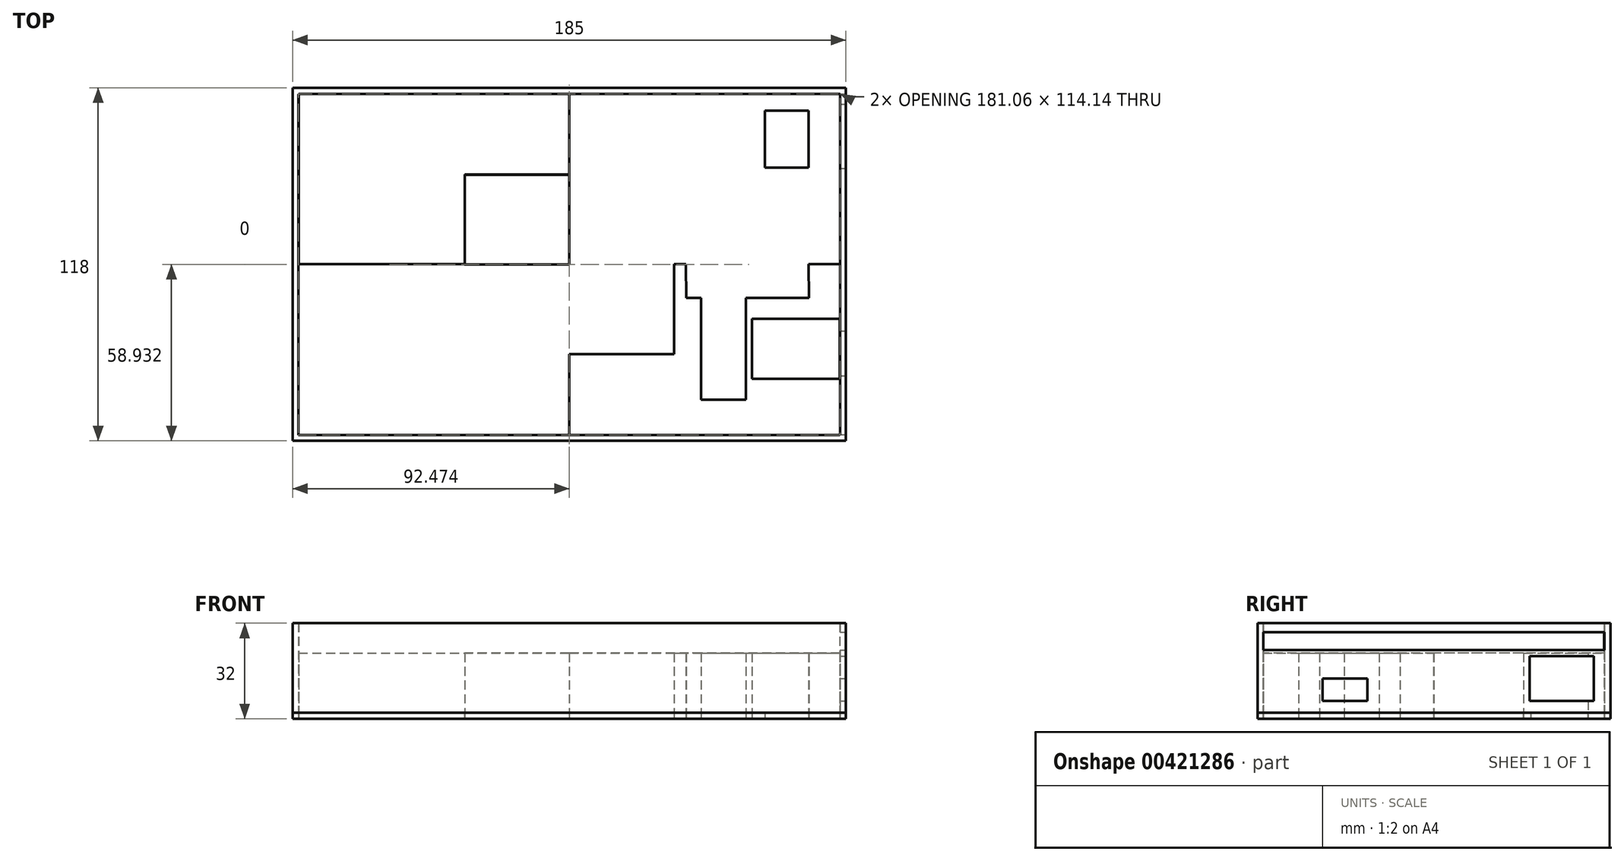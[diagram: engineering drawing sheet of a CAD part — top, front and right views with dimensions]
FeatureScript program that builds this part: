
annotation { "Feature Type Name" : "Feature", "Feature Type Description" : "" }
export const myFeature = defineFeature(function(context is Context, id is Id, definition is map)
    precondition{}
    {
        {
            var Q0;
            Q0=qCreatedBy(makeId("Top.planeOp"),FACE);
            var sketch = newSketch(context, id + "F0", { "sketchPlane" : qUnion([Q0])});
            skLineSegment(sketch, "E0.bottom", {"start": v(-155.12, 118) * mm, "end": v(29.88, 118) * mm});
            skLineSegment(sketch, "E0.top", {"start": v(-155.12, 0) * mm, "end": v(29.88, 0) * mm});
            skLineSegment(sketch, "E0.left", {"start": v(-155.12, 118) * mm, "end": v(-155.12, 0) * mm});
            skLineSegment(sketch, "E0.right", {"start": v(29.88, 118) * mm, "end": v(29.88, 0) * mm});
            skLineSegment(sketch, "E1.left", {"start": v(27.88, 108.58) * mm, "end": v(27.88, 9.42) * mm});
            skLineSegment(sketch, "E1.right", {"start": v(-153.12, 108.58) * mm, "end": v(-153.12, 9.42) * mm});
            skPoint(sketch, "E1.middle", {"position": v(-62.62, 59) * mm});
            skLineSegment(sketch, "E2", {"start": v(-153.12, 59) * mm, "end": v(-153.12, 116) * mm});
            skLineSegment(sketch, "E3", {"start": v(-153.12, 116) * mm, "end": v(27.88, 116) * mm});
            skLineSegment(sketch, "E4", {"start": v(27.88, 116) * mm, "end": v(27.88, 108.58) * mm});
            skLineSegment(sketch, "E5", {"start": v(-153.12, 59) * mm, "end": v(-153.12, 2) * mm});
            skLineSegment(sketch, "E6", {"start": v(-153.12, 2) * mm, "end": v(27.88, 2) * mm});
            skLineSegment(sketch, "E7", {"start": v(27.88, 2) * mm, "end": v(27.88, 9.42) * mm});
            skLineSegment(sketch, "E8.bottom", {"start": v(-153.17, 115.86) * mm, "end": v(27.83, 115.86) * mm});
            skLineSegment(sketch, "E8.top", {"start": v(-153.17, 1.86) * mm, "end": v(27.83, 1.86) * mm});
            skLineSegment(sketch, "E8.left", {"start": v(-153.17, 115.86) * mm, "end": v(-153.17, 1.86) * mm});
            skLineSegment(sketch, "E8.right", {"start": v(27.83, 115.86) * mm, "end": v(27.83, 1.86) * mm});
            skLineSegment(sketch, "E9", {"start": v(-153.17, 58.86) * mm, "end": v(27.83, 58.86) * mm});
            skLineSegment(sketch, "E10", {"start": v(-62.67, 1.86) * mm, "end": v(-62.67, 115.86) * mm});
            skLineSegment(sketch, "E11", {"start": v(-62.67, 1.86) * mm, "end": v(-62.67, 58.86) * mm});
            skPoint(sketch, "E12.middle", {"position": v(-62.67, 58.86) * mm});
            skLineSegment(sketch, "E13", {"start": v(-62.67, 58.86) * mm, "end": v(-27.67, 58.86) * mm});
            skLineSegment(sketch, "E14", {"start": v(-62.67, 58.86) * mm, "end": v(-62.67, 28.86) * mm});
            skLineSegment(sketch, "E15", {"start": v(-27.67, 28.86) * mm, "end": v(-27.67, 88.86) * mm});
            skLineSegment(sketch, "E16", {"start": v(-27.67, 88.86) * mm, "end": v(-97.67, 88.86) * mm});
            skLineSegment(sketch, "E17", {"start": v(-97.67, 88.86) * mm, "end": v(-97.67, 28.86) * mm});
            skLineSegment(sketch, "E18", {"start": v(-97.67, 28.86) * mm, "end": v(-27.67, 28.86) * mm});
            skLineSegment(sketch, "E19", {"start": v(-27.67, 58.86) * mm, "end": v(27.83, 58.86) * mm});
            skLineSegment(sketch, "E20", {"start": v(-23.67, 58.86) * mm, "end": v(-27.67, 58.86) * mm});
            skLineSegment(sketch, "E21", {"start": v(17.33, 58.86) * mm, "end": v(-23.67, 58.86) * mm});
            skLineSegment(sketch, "E22", {"start": v(17.33, 82.72) * mm, "end": v(17.33, 58.86) * mm});
            skLineSegment(sketch, "E23", {"start": v(-23.67, 58.86) * mm, "end": v(-23.67, 82.72) * mm});
            skLineSegment(sketch, "E24", {"start": v(-23.67, 82.72) * mm, "end": v(17.33, 82.72) * mm});
            skLineSegment(sketch, "E25", {"start": v(-18.54, 13.72) * mm, "end": v(-3.54, 13.72) * mm});
            skLineSegment(sketch, "E26", {"start": v(-18.54, 13.72) * mm, "end": v(-18.54, 47.72) * mm});
            skLineSegment(sketch, "E27", {"start": v(-18.54, 47.72) * mm, "end": v(-23.54, 47.72) * mm});
            skLineSegment(sketch, "E28", {"start": v(-23.54, 47.72) * mm, "end": v(-23.67, 58.86) * mm});
            skLineSegment(sketch, "E29", {"start": v(-3.54, 13.72) * mm, "end": v(-3.54, 47.72) * mm});
            skLineSegment(sketch, "E30", {"start": v(-3.54, 47.72) * mm, "end": v(17.46, 47.72) * mm});
            skLineSegment(sketch, "E31", {"start": v(17.46, 47.72) * mm, "end": v(17.33, 58.86) * mm});
            skLineSegment(sketch, "E32", {"start": v(17.46, 47.72) * mm, "end": v(29.88, 47.87) * mm});
            skLineSegment(sketch, "E33", {"start": v(-3.54, 47.72) * mm, "end": v(-1.54, 47.72) * mm});
            skLineSegment(sketch, "E34", {"start": v(-1.54, 30.72) * mm, "end": v(-1.54, 40.72) * mm});
            skLineSegment(sketch, "E35", {"start": v(-1.54, 20.72) * mm, "end": v(-1.54, 30.72) * mm});
            skLineSegment(sketch, "E36", {"start": v(-1.54, 20.72) * mm, "end": v(27.83, 20.72) * mm});
            skLineSegment(sketch, "E37", {"start": v(-1.54, 40.72) * mm, "end": v(27.83, 40.72) * mm});
            skLineSegment(sketch, "E38", {"start": v(27.83, 40.72) * mm, "end": v(27.83, 20.72) * mm});
            skLineSegment(sketch, "E39.left", {"start": v(-1.54, 40.72) * mm, "end": v(-1.54, 20.72) * mm});
            skLineSegment(sketch, "E40", {"start": v(17.33, 82.72) * mm, "end": v(17.33, 115.86) * mm});
            skLineSegment(sketch, "E41", {"start": v(27.88, 116) * mm, "end": v(27.83, 110.36) * mm});
            skLineSegment(sketch, "E42.bottom", {"start": v(27.83, 110.36) * mm, "end": v(2.83, 110.36) * mm});
            skLineSegment(sketch, "E42.top", {"start": v(27.83, 91.36) * mm, "end": v(2.83, 91.36) * mm});
            skLineSegment(sketch, "E42.left", {"start": v(27.83, 110.36) * mm, "end": v(27.83, 91.36) * mm});
            skLineSegment(sketch, "E42.right", {"start": v(2.83, 110.36) * mm, "end": v(2.83, 91.36) * mm});
            skSolve(sketch);
        }
        {
            var Q0;
            Q0=makeQuery(id+"F0.imprint","IMPRINT",FACE,{"disambiguationData":[TD([[makeQuery(id+"F0.imprint","IMPRINT",EDGE,{"derivedFrom":sQuery(id+"F0.wireOp",EDGE,"E0.bottom")}),-1.0]])]});
            var Q1;
            Q1=makeQuery(id+"F0.imprint","IMPRINT",FACE,{"disambiguationData":[TD([[makeQuery(id+"F0.imprint","IMPRINT",EDGE,{"derivedFrom":sQuery(id+"F0.wireOp",EDGE,"E37")}),-1.0]])]});
            var Q2;
            Q2=makeQuery(id+"F0.imprint","IMPRINT",FACE,{"disambiguationData":[TD([[makeQuery(id+"F0.imprint","IMPRINT",EDGE,{"derivedFrom":sQuery(id+"F0.wireOp",EDGE,"E21")}),1.0]])]});
            var Q3;
            Q3=makeQuery(id+"F0.imprint","IMPRINT",FACE,{"disambiguationData":[TD([[makeQuery(id+"F0.imprint","IMPRINT",EDGE,{"derivedFrom":sQuery(id+"F0.wireOp",EDGE,"E21")}),-1.0]])]});
            var Q4;
            {var subQ0=sQuery(id+"F0.wireOp",EDGE,"E13");Q4=makeQuery(id+"F0.imprint","IMPRINT",FACE,{"disambiguationData":[TD([[makeQuery(id+"F0.imprint","IMPRINT",EDGE,{"derivedFrom":subQ0}),1.0]])]});}
            var Q5;
            {var subQ3=sQuery(id+"F0.wireOp",EDGE,"E17");var subQ5=sQuery(id+"F0.wireOp",EDGE,"E16");var subQ6=makeQuery(id+"F0.imprint","INTERSECT",VERTEX,{"derivedFrom":[subQ5,subQ3]});Q5=makeQuery(id+"F0.imprint","IMPRINT",FACE,{"disambiguationData":[TD([[makeQuery(id+"F0.imprint","IMPRINT",EDGE,{"disambiguationData":[TD([[subQ6,1.0]])],"derivedFrom":subQ5}),1.0]])]});}
            var Q6;
            {var subQ0=sQuery(id+"F0.wireOp",EDGE,"E14");Q6=makeQuery(id+"F0.imprint","IMPRINT",FACE,{"disambiguationData":[TD([[makeQuery(id+"F0.imprint","IMPRINT",EDGE,{"derivedFrom":subQ0}),-1.0]])]});}
            var Q7;
            {var subQ0=sQuery(id+"F0.wireOp",EDGE,"E13");Q7=makeQuery(id+"F0.imprint","IMPRINT",FACE,{"disambiguationData":[TD([[makeQuery(id+"F0.imprint","IMPRINT",EDGE,{"derivedFrom":subQ0}),-1.0]])]});}
            var Q8;
            {var subQ5=sQuery(id+"F0.wireOp",EDGE,"E42.right");Q8=makeQuery(id+"F0.imprint","IMPRINT",FACE,{"disambiguationData":[TD([[makeQuery(id+"F0.imprint","IMPRINT",EDGE,{"derivedFrom":subQ5}),1.0]])]});}
            var Q9;
            {var subQ5=sQuery(id+"F0.wireOp",EDGE,"E42.left");Q9=makeQuery(id+"F0.imprint","IMPRINT",FACE,{"disambiguationData":[TD([[makeQuery(id+"F0.imprint","IMPRINT",EDGE,{"derivedFrom":subQ5}),-1.0]])]});}
            extrude(context, id + "F1", {"entities" : qUnion([Q0, Q1, Q2, Q3, Q4, Q5, Q6, Q7, Q8, Q9]), "depth" : 2 * mm});
        }
        {
            var Q0;
            Q0=qCreatedBy(makeId("Top.planeOp"),FACE);
            var sketch = newSketch(context, id + "F2", { "sketchPlane" : qUnion([Q0])});
            skLineSegment(sketch, "E43.bottom", {"start": v(-153.11, 116) * mm, "end": v(27.89, 116) * mm});
            skLineSegment(sketch, "E43.top", {"start": v(-153.11, 2) * mm, "end": v(27.89, 2) * mm});
            skLineSegment(sketch, "E43.left", {"start": v(-153.11, 116) * mm, "end": v(-153.11, 2) * mm});
            skLineSegment(sketch, "E43.right", {"start": v(27.89, 116) * mm, "end": v(27.89, 2) * mm});
            skLineSegment(sketch, "E44", {"start": v(-153.11, 59) * mm, "end": v(27.89, 59) * mm});
            skLineSegment(sketch, "E45", {"start": v(-62.61, 2) * mm, "end": v(-62.61, 116) * mm});
            skLineSegment(sketch, "E46", {"start": v(-62.61, 2) * mm, "end": v(-62.61, 59) * mm});
            skPoint(sketch, "E47.middle", {"position": v(-62.61, 59) * mm});
            skLineSegment(sketch, "E48", {"start": v(-62.61, 59) * mm, "end": v(-27.61, 59) * mm});
            skLineSegment(sketch, "E49", {"start": v(-62.61, 59) * mm, "end": v(-62.61, 29) * mm});
            skLineSegment(sketch, "E50", {"start": v(-27.61, 29) * mm, "end": v(-27.61, 89) * mm});
            skLineSegment(sketch, "E51", {"start": v(-27.61, 89) * mm, "end": v(-97.61, 89) * mm});
            skLineSegment(sketch, "E52", {"start": v(-97.61, 89) * mm, "end": v(-97.61, 29) * mm});
            skLineSegment(sketch, "E53", {"start": v(-97.61, 29) * mm, "end": v(-27.61, 29) * mm});
            skLineSegment(sketch, "E54", {"start": v(-27.61, 59) * mm, "end": v(27.89, 59) * mm});
            skLineSegment(sketch, "E55", {"start": v(-20.61, 59) * mm, "end": v(-27.61, 59) * mm});
            skLineSegment(sketch, "E56", {"start": v(20.39, 59) * mm, "end": v(-20.61, 59) * mm});
            skSolve(sketch);
        }
        {
            var Q0;
            {var subQ1=sQuery(id+"F2.wireOp",EDGE,"E43.bottom");var subQ5=sQuery(id+"F2.wireOp",EDGE,"E43.left");var subQ6=makeQuery(id+"F2.imprint","INTERSECT",VERTEX,{"derivedFrom":[subQ1,subQ5]});Q0=makeQuery(id+"F2.imprint","IMPRINT",FACE,{"disambiguationData":[TD([[makeQuery(id+"F2.imprint","IMPRINT",EDGE,{"disambiguationData":[TD([[subQ6,-1.0]])],"derivedFrom":subQ1}),-1.0]])]});}
            var Q1;
            {var subQ7=sQuery(id+"F2.wireOp",EDGE,"E46");Q1=makeQuery(id+"F2.imprint","IMPRINT",FACE,{"disambiguationData":[TD([[makeQuery(id+"F2.imprint","IMPRINT",EDGE,{"derivedFrom":subQ7}),1.0]])]});}
            extrude(context, id + "F3", {"entities" : qUnion([Q0, Q1]), "depth" : 22 * mm});
        }
        {
            var Q0;
            Q0=makeQuery(id+"F1.opExtrude","CAP_FACE",FACE,{"disambiguationData":[OSD([sQuery(id+"F0.wireOp",EDGE,"E0.bottom"),sQuery(id+"F0.wireOp",EDGE,"E0.top"),sQuery(id+"F0.wireOp",EDGE,"E0.left"),sQuery(id+"F0.wireOp",EDGE,"E0.right"),sQuery(id+"F0.wireOp",EDGE,"E1.left"),sQuery(id+"F0.wireOp",EDGE,"E2"),sQuery(id+"F0.wireOp",EDGE,"E3"),sQuery(id+"F0.wireOp",EDGE,"E4"),sQuery(id+"F0.wireOp",EDGE,"E6"),sQuery(id+"F0.wireOp",EDGE,"E7"),sQuery(id+"F0.wireOp",EDGE,"E8.bottom"),sQuery(id+"F0.wireOp",EDGE,"E8.top"),sQuery(id+"F0.wireOp",EDGE,"E8.left"),sQuery(id+"F0.wireOp",EDGE,"E8.right")])],"isStart":false});
            extrude(context, id + "F4", {"entities" : qUnion([Q0]), "depth" : 30 * mm});
        }
        {
            var Q0;
            Q0=makeQuery(id+"F1.opExtrude","CAP_FACE",FACE,{"disambiguationData":[OSD([sQuery(id+"F0.wireOp",EDGE,"E0.bottom"),sQuery(id+"F0.wireOp",EDGE,"E0.top"),sQuery(id+"F0.wireOp",EDGE,"E0.left"),sQuery(id+"F0.wireOp",EDGE,"E0.right"),sQuery(id+"F0.wireOp",EDGE,"E1.left"),sQuery(id+"F0.wireOp",EDGE,"E2"),sQuery(id+"F0.wireOp",EDGE,"E3"),sQuery(id+"F0.wireOp",EDGE,"E4"),sQuery(id+"F0.wireOp",EDGE,"E6"),sQuery(id+"F0.wireOp",EDGE,"E7"),sQuery(id+"F0.wireOp",EDGE,"E8.bottom"),sQuery(id+"F0.wireOp",EDGE,"E8.top"),sQuery(id+"F0.wireOp",EDGE,"E8.left"),sQuery(id+"F0.wireOp",EDGE,"E8.right")])],"isStart":true});
            var sketch = newSketch(context, id + "F5", { "sketchPlane" : qUnion([Q0])});
            skLineSegment(sketch, "E57.0.0", {"start": v(-62.61, -89) * mm, "end": v(-62.61, -59) * mm});
            skLineSegment(sketch, "E57.0.1", {"start": v(-62.61, -59) * mm, "end": v(-27.61, -59) * mm});
            skLineSegment(sketch, "E57.0.2", {"start": v(-27.61, -59) * mm, "end": v(-27.61, -89) * mm});
            skLineSegment(sketch, "E57.0.3", {"start": v(-27.61, -89) * mm, "end": v(-62.61, -89) * mm});
            skLineSegment(sketch, "E58.0.0", {"start": v(-62.61, -29) * mm, "end": v(-27.61, -29) * mm});
            skLineSegment(sketch, "E58.0.1", {"start": v(-27.61, -29) * mm, "end": v(-27.61, -59) * mm});
            skLineSegment(sketch, "E58.0.2", {"start": v(-27.61, -59) * mm, "end": v(-62.61, -59) * mm});
            skLineSegment(sketch, "E58.0.3", {"start": v(-62.61, -59) * mm, "end": v(-62.61, -29) * mm});
            skLineSegment(sketch, "E59.0.0", {"start": v(-62.61, -59) * mm, "end": v(-97.61, -59) * mm});
            skLineSegment(sketch, "E59.0.1", {"start": v(-97.61, -59) * mm, "end": v(-97.61, -29) * mm});
            skLineSegment(sketch, "E59.0.2", {"start": v(-97.61, -29) * mm, "end": v(-62.61, -29) * mm});
            skLineSegment(sketch, "E59.0.3", {"start": v(-62.61, -29) * mm, "end": v(-62.61, -59) * mm});
            skLineSegment(sketch, "E60.0.0", {"start": v(-62.61, -89) * mm, "end": v(-97.61, -89) * mm});
            skLineSegment(sketch, "E60.0.1", {"start": v(-97.61, -89) * mm, "end": v(-97.61, -59) * mm});
            skLineSegment(sketch, "E60.0.2", {"start": v(-97.61, -59) * mm, "end": v(-62.61, -59) * mm});
            skLineSegment(sketch, "E60.0.3", {"start": v(-62.61, -59) * mm, "end": v(-62.61, -89) * mm});
            skLineSegment(sketch, "E61.0.0", {"start": v(-62.61, -116) * mm, "end": v(-62.61, -89) * mm});
            skLineSegment(sketch, "E61.0.1", {"start": v(-62.61, -89) * mm, "end": v(-27.61, -89) * mm});
            skLineSegment(sketch, "E61.0.2", {"start": v(-27.61, -89) * mm, "end": v(-27.61, -59) * mm});
            skLineSegment(sketch, "E61.0.3", {"start": v(-27.61, -59) * mm, "end": v(-20.61, -59) * mm});
            skLineSegment(sketch, "E61.0.4", {"start": v(-20.61, -59) * mm, "end": v(20.39, -59) * mm});
            skLineSegment(sketch, "E61.0.5", {"start": v(20.39, -59) * mm, "end": v(27.89, -59) * mm});
            skLineSegment(sketch, "E61.0.6", {"start": v(27.89, -59) * mm, "end": v(27.89, -116) * mm});
            skLineSegment(sketch, "E61.0.7", {"start": v(27.89, -116) * mm, "end": v(-62.61, -116) * mm});
            skLineSegment(sketch, "E62.0", {"start": v(-23.67, -82.72) * mm, "end": v(17.33, -82.72) * mm});
            skLineSegment(sketch, "E63.0", {"start": v(-23.67, -58.86) * mm, "end": v(-23.67, -82.72) * mm});
            skLineSegment(sketch, "E64.0", {"start": v(-23.54, -47.72) * mm, "end": v(-23.67, -58.86) * mm});
            skPoint(sketch, "E65.0", {"position": v(-21.04, -47.72) * mm});
            skLineSegment(sketch, "E66.0", {"start": v(-18.54, -13.72) * mm, "end": v(-18.54, -47.72) * mm});
            skLineSegment(sketch, "E67.0", {"start": v(-18.54, -47.72) * mm, "end": v(-23.54, -47.72) * mm});
            skLineSegment(sketch, "E68.0", {"start": v(-18.54, -13.72) * mm, "end": v(-3.54, -13.72) * mm});
            skLineSegment(sketch, "E69.0", {"start": v(-3.54, -13.72) * mm, "end": v(-3.54, -47.72) * mm});
            skLineSegment(sketch, "E70.0", {"start": v(-1.54, -40.72) * mm, "end": v(-1.54, -20.72) * mm});
            skLineSegment(sketch, "E71.0", {"start": v(-1.54, -20.72) * mm, "end": v(27.83, -20.72) * mm});
            skLineSegment(sketch, "E72.0", {"start": v(-1.54, -40.72) * mm, "end": v(27.83, -40.72) * mm});
            skLineSegment(sketch, "E73.0", {"start": v(-3.54, -47.72) * mm, "end": v(17.46, -47.72) * mm});
            skLineSegment(sketch, "E74.0", {"start": v(17.46, -47.72) * mm, "end": v(17.33, -58.86) * mm});
            skLineSegment(sketch, "E75.0", {"start": v(17.33, -82.72) * mm, "end": v(17.33, -58.86) * mm});
            skLineSegment(sketch, "E76", {"start": v(-62.62, -1.86) * mm, "end": v(-62.61, -116) * mm});
            skPoint(sketch, "E76.startSnap0", {"position": v(-62.62, 0) * mm});
            skLineSegment(sketch, "E77.bottom", {"start": v(27.83, -40.72) * mm, "end": v(-1.54, -40.72) * mm});
            skLineSegment(sketch, "E77.top", {"start": v(27.83, -20.72) * mm, "end": v(-1.54, -20.72) * mm});
            skLineSegment(sketch, "E77.left", {"start": v(27.83, -40.72) * mm, "end": v(27.83, -20.72) * mm});
            skLineSegment(sketch, "E78", {"start": v(27.89, -116) * mm, "end": v(27.88, -110.5) * mm});
            skLineSegment(sketch, "E79.bottom", {"start": v(27.88, -110.5) * mm, "end": v(2.88, -110.5) * mm});
            skLineSegment(sketch, "E79.top", {"start": v(27.88, -91.5) * mm, "end": v(2.88, -91.5) * mm});
            skLineSegment(sketch, "E79.left", {"start": v(27.88, -110.5) * mm, "end": v(27.88, -91.5) * mm});
            skLineSegment(sketch, "E79.right", {"start": v(2.88, -110.5) * mm, "end": v(2.88, -91.5) * mm});
            skSolve(sketch);
        }
        {
            var Q0;
            {var subQ1=sQuery(id+"F5.wireOp",EDGE,"E58.0.0");Q0=makeQuery(id+"F5.imprint","IMPRINT",FACE,{"disambiguationData":[TD([[makeQuery(id+"F5.imprint","IMPRINT",EDGE,{"derivedFrom":subQ1}),1.0]])]});}
            var Q1;
            {var subQ9=sQuery(id+"F5.wireOp",EDGE,"E61.0.0");Q1=makeQuery(id+"F5.imprint","IMPRINT",FACE,{"disambiguationData":[TD([[makeQuery(id+"F5.imprint","IMPRINT",EDGE,{"derivedFrom":subQ9}),-1.0]])]});}
            extrude(context, id + "F6", {"entities" : qUnion([Q0, Q1]), "oppositeDirection" : true, "depth" : 22 * mm});
        }
        {
            var Q0;
            Q0=makeQuery(id+"F4.opExtrude","SWEPT_FACE",FACE,{"disambiguationData":[OSD([sQuery(id+"F0.wireOp",EDGE,"E0.right")])]});
            var sketch = newSketch(context, id + "F7", { "sketchPlane" : qUnion([Q0])});
            skLineSegment(sketch, "E80", {"start": v(0, 2) * mm, "end": v(21.72, 2) * mm});
            skLineSegment(sketch, "E81", {"start": v(21.72, 2) * mm, "end": v(21.72, 6) * mm});
            skLineSegment(sketch, "E82.bottom", {"start": v(21.72, 6) * mm, "end": v(36.72, 6) * mm});
            skLineSegment(sketch, "E82.top", {"start": v(21.72, 13.5) * mm, "end": v(36.72, 13.5) * mm});
            skLineSegment(sketch, "E82.left", {"start": v(21.72, 6) * mm, "end": v(21.72, 13.5) * mm});
            skLineSegment(sketch, "E82.right", {"start": v(36.72, 6) * mm, "end": v(36.72, 13.5) * mm});
            skLineSegment(sketch, "E83", {"start": v(118, 2) * mm, "end": v(118, 32) * mm});
            skLineSegment(sketch, "E84", {"start": v(118, 2) * mm, "end": v(118, 23) * mm});
            skLineSegment(sketch, "E85", {"start": v(118, 23) * mm, "end": v(116, 23) * mm});
            skLineSegment(sketch, "E86", {"start": v(0, 23) * mm, "end": v(2, 23) * mm});
            skLineSegment(sketch, "E87.bottom", {"start": v(2, 23) * mm, "end": v(116, 23) * mm});
            skLineSegment(sketch, "E87.top", {"start": v(2, 29) * mm, "end": v(116, 29) * mm});
            skLineSegment(sketch, "E87.left", {"start": v(2, 23) * mm, "end": v(2, 29) * mm});
            skLineSegment(sketch, "E87.right", {"start": v(116, 23) * mm, "end": v(116, 29) * mm});
            skLineSegment(sketch, "E88", {"start": v(118, 2) * mm, "end": v(118, 6) * mm});
            skLineSegment(sketch, "E89", {"start": v(118, 6) * mm, "end": v(112.5, 6) * mm});
            skLineSegment(sketch, "E90.bottom", {"start": v(112.5, 6) * mm, "end": v(91, 6) * mm});
            skLineSegment(sketch, "E90.top", {"start": v(112.5, 21) * mm, "end": v(91, 21) * mm});
            skLineSegment(sketch, "E90.left", {"start": v(112.5, 6) * mm, "end": v(112.5, 21) * mm});
            skLineSegment(sketch, "E90.right", {"start": v(91, 6) * mm, "end": v(91, 21) * mm});
            skLineSegment(sketch, "E91", {"start": v(2, 29) * mm, "end": v(7, 29) * mm});
            skLineSegment(sketch, "E92", {"start": v(7, 29) * mm, "end": v(9, 29) * mm});
            skLineSegment(sketch, "E93", {"start": v(9, 29) * mm, "end": v(14, 29) * mm});
            skLineSegment(sketch, "E94", {"start": v(14, 29) * mm, "end": v(16, 29) * mm});
            skLineSegment(sketch, "E95", {"start": v(16, 29) * mm, "end": v(21, 29) * mm});
            skLineSegment(sketch, "E96", {"start": v(21, 29) * mm, "end": v(23, 29) * mm});
            skLineSegment(sketch, "E97", {"start": v(23, 29) * mm, "end": v(28, 29) * mm});
            skLineSegment(sketch, "E98", {"start": v(28, 29) * mm, "end": v(30, 29) * mm});
            skLineSegment(sketch, "E99", {"start": v(30, 29) * mm, "end": v(35, 29) * mm});
            skLineSegment(sketch, "E100", {"start": v(35, 29) * mm, "end": v(37, 29) * mm});
            skLineSegment(sketch, "E101", {"start": v(37, 29) * mm, "end": v(42, 29) * mm});
            skLineSegment(sketch, "E102", {"start": v(42, 29) * mm, "end": v(44, 29) * mm});
            skLineSegment(sketch, "E103", {"start": v(44, 29) * mm, "end": v(49, 29) * mm});
            skLineSegment(sketch, "E104", {"start": v(49, 29) * mm, "end": v(51, 29) * mm});
            skLineSegment(sketch, "E105", {"start": v(51, 29) * mm, "end": v(56, 29) * mm});
            skLineSegment(sketch, "E106", {"start": v(56, 29) * mm, "end": v(58, 29) * mm});
            skLineSegment(sketch, "E107", {"start": v(58, 29) * mm, "end": v(63, 29) * mm});
            skLineSegment(sketch, "E108", {"start": v(63, 29) * mm, "end": v(65, 29) * mm});
            skLineSegment(sketch, "E109", {"start": v(65, 29) * mm, "end": v(70, 29) * mm});
            skLineSegment(sketch, "E110", {"start": v(70, 29) * mm, "end": v(72, 29) * mm});
            skLineSegment(sketch, "E111", {"start": v(72, 29) * mm, "end": v(77, 29) * mm});
            skLineSegment(sketch, "E112", {"start": v(77, 29) * mm, "end": v(79, 29) * mm});
            skLineSegment(sketch, "E113", {"start": v(79, 29) * mm, "end": v(84, 29) * mm});
            skLineSegment(sketch, "E114", {"start": v(84, 29) * mm, "end": v(86, 29) * mm});
            skLineSegment(sketch, "E115", {"start": v(86, 29) * mm, "end": v(91, 29) * mm});
            skLineSegment(sketch, "E116", {"start": v(91, 29) * mm, "end": v(93, 29) * mm});
            skLineSegment(sketch, "E117", {"start": v(93, 29) * mm, "end": v(98, 29) * mm});
            skLineSegment(sketch, "E118", {"start": v(98, 29) * mm, "end": v(100, 29) * mm});
            skLineSegment(sketch, "E119", {"start": v(100, 29) * mm, "end": v(105, 29) * mm});
            skLineSegment(sketch, "E120", {"start": v(105, 29) * mm, "end": v(107, 29) * mm});
            skLineSegment(sketch, "E121", {"start": v(107, 29) * mm, "end": v(112, 29) * mm});
            skLineSegment(sketch, "E122", {"start": v(112, 29) * mm, "end": v(114, 29) * mm});
            skLineSegment(sketch, "E123.top", {"start": v(7, 23) * mm, "end": v(9, 23) * mm});
            skLineSegment(sketch, "E123.left", {"start": v(7, 29) * mm, "end": v(7, 23) * mm});
            skLineSegment(sketch, "E123.right", {"start": v(9, 29) * mm, "end": v(9, 23) * mm});
            skLineSegment(sketch, "E124.top", {"start": v(14, 23) * mm, "end": v(16, 23) * mm});
            skLineSegment(sketch, "E124.left", {"start": v(14, 29) * mm, "end": v(14, 23) * mm});
            skLineSegment(sketch, "E124.right", {"start": v(16, 29) * mm, "end": v(16, 23) * mm});
            skLineSegment(sketch, "E125.top", {"start": v(21, 23) * mm, "end": v(23, 23) * mm});
            skLineSegment(sketch, "E125.left", {"start": v(21, 29) * mm, "end": v(21, 23) * mm});
            skLineSegment(sketch, "E125.right", {"start": v(23, 29) * mm, "end": v(23, 23) * mm});
            skLineSegment(sketch, "E126.top", {"start": v(28, 23) * mm, "end": v(30, 23) * mm});
            skLineSegment(sketch, "E126.left", {"start": v(28, 29) * mm, "end": v(28, 23) * mm});
            skLineSegment(sketch, "E126.right", {"start": v(30, 29) * mm, "end": v(30, 23) * mm});
            skLineSegment(sketch, "E127.top", {"start": v(35, 23) * mm, "end": v(37, 23) * mm});
            skLineSegment(sketch, "E127.left", {"start": v(35, 29) * mm, "end": v(35, 23) * mm});
            skLineSegment(sketch, "E127.right", {"start": v(37, 29) * mm, "end": v(37, 23) * mm});
            skLineSegment(sketch, "E128.top", {"start": v(42, 23) * mm, "end": v(44, 23) * mm});
            skLineSegment(sketch, "E128.left", {"start": v(42, 29) * mm, "end": v(42, 23) * mm});
            skLineSegment(sketch, "E128.right", {"start": v(44, 29) * mm, "end": v(44, 23) * mm});
            skLineSegment(sketch, "E129.top", {"start": v(49, 23) * mm, "end": v(51, 23) * mm});
            skLineSegment(sketch, "E129.left", {"start": v(49, 29) * mm, "end": v(49, 23) * mm});
            skLineSegment(sketch, "E129.right", {"start": v(51, 29) * mm, "end": v(51, 23) * mm});
            skLineSegment(sketch, "E130.top", {"start": v(56, 23) * mm, "end": v(58, 23) * mm});
            skLineSegment(sketch, "E130.left", {"start": v(56, 29) * mm, "end": v(56, 23) * mm});
            skLineSegment(sketch, "E130.right", {"start": v(58, 29) * mm, "end": v(58, 23) * mm});
            skLineSegment(sketch, "E131.top", {"start": v(63, 23) * mm, "end": v(65, 23) * mm});
            skLineSegment(sketch, "E131.left", {"start": v(63, 29) * mm, "end": v(63, 23) * mm});
            skLineSegment(sketch, "E131.right", {"start": v(65, 29) * mm, "end": v(65, 23) * mm});
            skLineSegment(sketch, "E132.top", {"start": v(70, 23) * mm, "end": v(72, 23) * mm});
            skLineSegment(sketch, "E132.left", {"start": v(70, 29) * mm, "end": v(70, 23) * mm});
            skLineSegment(sketch, "E132.right", {"start": v(72, 29) * mm, "end": v(72, 23) * mm});
            skLineSegment(sketch, "E133.top", {"start": v(77, 23) * mm, "end": v(79, 23) * mm});
            skLineSegment(sketch, "E133.left", {"start": v(77, 29) * mm, "end": v(77, 23) * mm});
            skLineSegment(sketch, "E133.right", {"start": v(79, 29) * mm, "end": v(79, 23) * mm});
            skLineSegment(sketch, "E134.top", {"start": v(84, 23) * mm, "end": v(86, 23) * mm});
            skLineSegment(sketch, "E134.left", {"start": v(84, 29) * mm, "end": v(84, 23) * mm});
            skLineSegment(sketch, "E134.right", {"start": v(86, 29) * mm, "end": v(86, 23) * mm});
            skLineSegment(sketch, "E135.top", {"start": v(91, 23) * mm, "end": v(93, 23) * mm});
            skLineSegment(sketch, "E135.left", {"start": v(91, 29) * mm, "end": v(91, 23) * mm});
            skLineSegment(sketch, "E135.right", {"start": v(93, 29) * mm, "end": v(93, 23) * mm});
            skLineSegment(sketch, "E136.top", {"start": v(98, 23) * mm, "end": v(100, 23) * mm});
            skLineSegment(sketch, "E136.left", {"start": v(98, 29) * mm, "end": v(98, 23) * mm});
            skLineSegment(sketch, "E136.right", {"start": v(100, 29) * mm, "end": v(100, 23) * mm});
            skLineSegment(sketch, "E137.top", {"start": v(105, 23) * mm, "end": v(107, 23) * mm});
            skLineSegment(sketch, "E137.left", {"start": v(105, 29) * mm, "end": v(105, 23) * mm});
            skLineSegment(sketch, "E137.right", {"start": v(107, 29) * mm, "end": v(107, 23) * mm});
            skLineSegment(sketch, "E138.top", {"start": v(112, 23) * mm, "end": v(114, 23) * mm});
            skLineSegment(sketch, "E138.left", {"start": v(112, 29) * mm, "end": v(112, 23) * mm});
            skLineSegment(sketch, "E138.right", {"start": v(114, 29) * mm, "end": v(114, 23) * mm});
            skSolve(sketch);
        }
        {
            var Q0;
            Q0=makeQuery(id+"F7.imprint","IMPRINT",FACE,{"disambiguationData":[TD([[makeQuery(id+"F7.imprint","IMPRINT",EDGE,{"derivedFrom":sQuery(id+"F7.wireOp",EDGE,"E87.bottom")}),1.0]])]});
            var Q1;
            Q1=makeQuery(id+"F7.imprint","IMPRINT",FACE,{"disambiguationData":[TD([[makeQuery(id+"F7.imprint","IMPRINT",EDGE,{"derivedFrom":sQuery(id+"F7.wireOp",EDGE,"E82.bottom")}),1.0]])]});
            var Q2;
            Q2=makeQuery(id+"F7.imprint","IMPRINT",FACE,{"disambiguationData":[TD([[makeQuery(id+"F7.imprint","IMPRINT",EDGE,{"derivedFrom":sQuery(id+"F7.wireOp",EDGE,"E90.bottom")}),-1.0]])]});
            extrude(context, id + "F8", {"entities" : qUnion([Q0, Q1, Q2]), "operationType" : NewBodyOperationType.REMOVE, "oppositeDirection" : true, "depth" : 2 * mm});
        }
    });
